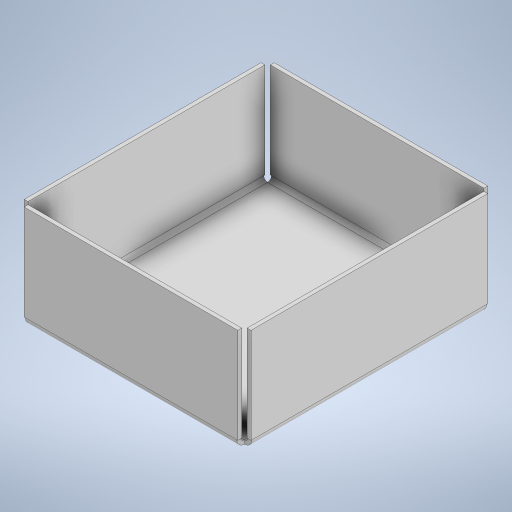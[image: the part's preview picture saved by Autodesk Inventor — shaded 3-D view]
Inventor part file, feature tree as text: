
AUTODESK INVENTOR PART (.ipt)
format: ipt  version: 2024.3 (Build 283343000, 343)  size: 242,688 bytes
history: native  units: mm
features: sheet_metal_op x4, sketch x2, other x2
ambient origin geometry x8: Origin, YZ Plane, XZ Plane, XY Plane, X Axis, Y Axis, Z Axis, Center Point
bodies: Solid1 (feature_tree)
feature tree (8):
  sheet_metal_op  "Face1"
  sheet_metal_op  "Flange1"
  sketch  "Sketch1"  dims[d0=97.0mm]
  other  "Plate1"
  sketch  "Sketch2"  dims[d1=88.0mm d2=1.5mm d3=1.5mm d4=0.75mm d5=3.0mm d6=1.5mm d7=40.0mm d8=90.0deg d9=1.5mm d10=6.0mm d11=1.5mm d12=1.5mm]
  other  "Plate2"
  sheet_metal_op  "Bend1"
  sheet_metal_op  "Corner1"
